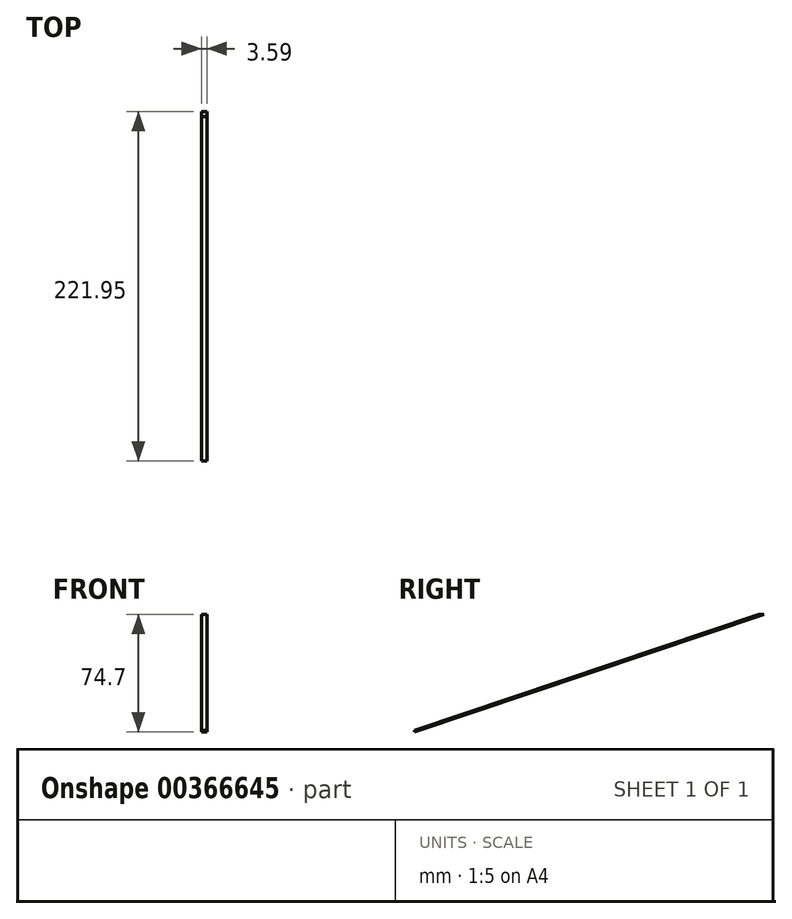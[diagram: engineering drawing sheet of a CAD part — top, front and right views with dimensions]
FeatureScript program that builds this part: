
annotation { "Feature Type Name" : "Feature", "Feature Type Description" : "" }
export const myFeature = defineFeature(function(context is Context, id is Id, definition is map)
    precondition{}
    {
        {
            var Q0;
            Q0=qCreatedBy(makeId("Top.planeOp"),FACE);
            var sketch = newSketch(context, id + "F0", { "sketchPlane" : qUnion([Q0])});
            skLineSegment(sketch, "E0.bottom", {"start": v(0, -74.64) * mm, "end": v(-2.4, -74.64) * mm});
            skLineSegment(sketch, "E0.top", {"start": v(0, 74.6) * mm, "end": v(-2.4, 74.6) * mm});
            skLineSegment(sketch, "E0.left", {"start": v(0, -74.64) * mm, "end": v(0, 74.6) * mm});
            skLineSegment(sketch, "E0.right", {"start": v(-2.4, -74.64) * mm, "end": v(-2.4, 74.6) * mm});
            skSolve(sketch);
        }
        {
            var Q0;
            Q0 = qSketchRegion(id + "F0", true);
            extrude(context, id + "F1", {"entities" : qUnion([Q0]), "depth" : 54 * mm});
        }
        {
            var Q0;
            Q0=makeQuery(id+"F1.opExtrude","SWEPT_FACE",FACE,{"disambiguationData":[OSD([sQuery(id+"F0.wireOp",EDGE,"E0.left")])]});
            var sketch = newSketch(context, id + "F2", { "sketchPlane" : qUnion([Q0])});
            skLineSegment(sketch, "E1", {"start": v(-74.64, 4.95) * mm, "end": v(71.1, 54) * mm});
            skLineSegment(sketch, "E2", {"start": v(73.33, 54) * mm, "end": v(-74.64, 4.2) * mm});
            skSolve(sketch);
        }
        {
            var Q0;
            {var subQ0=sQuery(id+"F2.wireOp",EDGE,"E1");Q0=makeQuery(id+"F2.imprint","IMPRINT",FACE,{"disambiguationData":[TD([[makeQuery(id+"F2.imprint","IMPRINT",EDGE,{"derivedFrom":subQ0}),1.0]])]});}
            var Q1;
            {var subQ3=sQuery(id+"F2.wireOp",EDGE,"E2");Q1=makeQuery(id+"F2.imprint","IMPRINT",FACE,{"disambiguationData":[TD([[makeQuery(id+"F2.imprint","IMPRINT",EDGE,{"derivedFrom":subQ3}),1.0]])]});}
            extrude(context, id + "F3", {"entities" : qUnion([Q0, Q1]), "operationType" : NewBodyOperationType.REMOVE, "oppositeDirection" : true, "depth" : 25 * mm});
        }
        {
            var Q0;
            Q0=makeQuery(id+"F1.opExtrude","SWEPT_BODY",BODY,{"disambiguationData":[OSD([sQuery(id+"F0.wireOp",EDGE,"E0.bottom"),sQuery(id+"F0.wireOp",EDGE,"E0.top"),sQuery(id+"F0.wireOp",EDGE,"E0.left"),sQuery(id+"F0.wireOp",EDGE,"E0.right")])]});
            var Q1;
            Q1=makeQuery(id+"F3.boolean.opBoolean","COPY",VERTEX,{"derivedFrom":makeQuery(id+"F3.opExtrude","CAP_VERTEX",VERTEX,{"disambiguationData":[OSD([sQuery(id+"F0.wireOp",EDGE,"E0.bottom"),sQuery(id+"F0.wireOp",EDGE,"E0.left"),sQuery(id+"F2.wireOp",EDGE,"E2")])],"isStart":true})});
            transform(context, id + "F4", {"entities" : qUnion([Q0]), "transformType" : TransformType.SCALE_UNIFORMLY, "scale" : 1.5, "scalePoint" : qUnion([Q1]), "makeCopy" : false});
        }
    });
